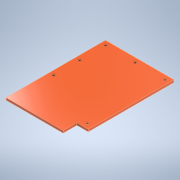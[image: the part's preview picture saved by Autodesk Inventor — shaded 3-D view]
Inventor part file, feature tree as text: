
AUTODESK INVENTOR PART (.ipt)
format: ipt  version: 2021 (Build 250183000, 183)  size: 136,704 bytes
history: native  units: mm
features: sketch x3, extrude x2, hole x1
ambient origin geometry x8: Origin, YZ Plane, XZ Plane, XY Plane, X Axis, Y Axis, Z Axis, Center Point
bodies: Solid1 (feature_tree)
feature tree (6):
  extrude  "Extrusion1"  Depth=112.5mm
  extrude  "Extrusion2"  Depth=15.0mm
  hole  "Hole1"  [1 undecoded]
  sketch  "Sketch1"  dims[d0=90.0mm d1=112.5mm]
  sketch  "Sketch3"  dims[d2=3.0mm d3=0.0mm d5=15.0mm]
  sketch  "Sketch4"  dims[d6=18.0mm d7=0.0mm d8=6.0mm d9=6.0mm d10=6.0mm d11=6.0mm d12=7.5mm d13=39.0mm d14=34.0mm d15=34.0mm d16=3.2mm d17=6.0mm d18=4.0mm d19=2.0mm d20=90.0deg d21=9.0mm d22=20.594885mm]
note: 1 required parameter value undecoded (feature->parameter linkage not recoverable at this tier; creation-order binding heuristic only, values carry confidence <= 0.55)
